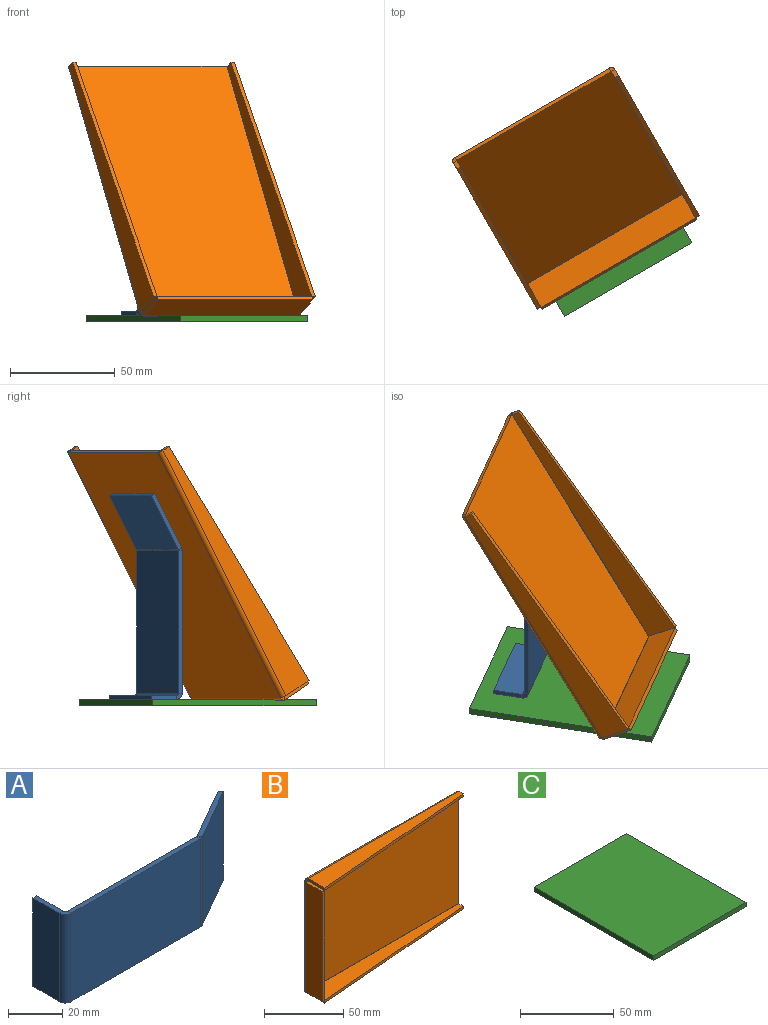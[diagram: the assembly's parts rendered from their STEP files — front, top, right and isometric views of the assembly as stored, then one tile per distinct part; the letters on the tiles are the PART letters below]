
ASSEMBLY  parts=3 mates=2
PART A: 22 faces, bbox 98x17x40 mm
  f0: plane 67.73x2mm, normal (0,0,1), area 135.5mm2, adj f2,f3,f10,f19
  f1: plane 67.73x2mm, normal (0,0,-1), area 135.5mm2, adj f2,f3,f9,f18
  f2: plane 67.73x40mm, normal (0,-1,0), area 2709.3mm2, adj f0,f1,f11,f20
  f3: plane 67.73x40mm, normal (0,1,0), area 2709.3mm2, adj f0,f1,f12,f21
  f4: plane 26.75x16.6mm, normal (0,0,1), area 59.5mm2, adj f6,f7,f8,f10
  f5: plane 26.75x16.6mm, normal (0,0,-1), area 59.5mm2, adj f6,f7,f8,f9
  f6: plane 40x1.73mm, normal (0.87,0.5,0), area 80mm2, adj f4,f5,f7,f8
  f7: plane 40x25.75mm, normal (0.5,-0.87,0), area 1189.3mm2, adj f4,f5,f6,f11
  f8: plane 40x25.75mm, normal (-0.5,0.87,0), area 1189.3mm2, adj f4,f5,f6,f12
  f9: plane 2.13x1.5mm, normal (0,0,-1), area 2.1mm2, adj f1,f5,f11,f12
  f10: plane 2.13x1.5mm, normal (0,0,1), area 2.1mm2, adj f0,f4,f11,f12
  f11: cylinder r=3mm len=40mm, axis (0,0,-1), area 62.8mm2, adj f2,f7,f9,f10
  f12: cylinder r=1mm len=40mm, axis (0,0,-1), area 20.9mm2, adj f3,f8,f9,f10
  f13: plane 14x2mm, normal (0,0,1), area 28mm2, adj f14,f16,f17,f19
  f14: plane 40x2mm, normal (0,1,0), area 80mm2, adj f13,f15,f16,f17
  f15: plane 14x2mm, normal (0,0,-1), area 28mm2, adj f14,f16,f17,f18
  f16: plane 40x14mm, normal (-1,0,0), area 560mm2, adj f13,f14,f15,f20
  f17: plane 40x14mm, normal (1,0,0), area 560mm2, adj f13,f14,f15,f21
  f18: plane 3x3mm, normal (0,0,-1), area 6.3mm2, adj f1,f15,f20,f21
  f19: plane 3x3mm, normal (0,0,1), area 6.3mm2, adj f0,f13,f20,f21
  f20: cylinder r=3mm len=40mm, axis (0,0,-1), area 188.5mm2, adj f2,f16,f18,f19
  f21: cylinder r=1mm len=40mm, axis (0,0,-1), area 62.8mm2, adj f3,f17,f18,f19
PART B: 34 faces, bbox 137x17x89 mm
  f0: plane 2x0.08mm, normal (0,1,0), area 0.2mm2, adj f1,f4,f5,f31
  f1: plane 14.9x2mm, normal (-1,0,0), area 29.8mm2, adj f0,f3,f4,f5
  f2: plane 3.9x2mm, normal (1,0,0), area 7.8mm2, adj f3,f4,f5,f30
  f3: plane 134.98x11mm, normal (0.08,-1,0), area 270.9mm2, adj f1,f2,f4,f5
  f4: plane 134.98x14.9mm, normal (0,0,-1), area 1268.8mm2, adj f0,f1,f2,f3,f32
  f5: plane 134.98x14.9mm, normal (0,0,1), area 1268.8mm2, adj f0,f1,f2,f3,f33
  f6: plane 3.9x2mm, normal (1,0,0), area 7.8mm2, adj f9,f10,f11,f26
  f7: plane 2x0.08mm, normal (0,1,0), area 0.2mm2, adj f8,f10,f11,f27
  f8: plane 14.9x2mm, normal (-1,0,0), area 29.8mm2, adj f7,f9,f10,f11
  f9: plane 134.98x11mm, normal (0.08,-1,0), area 270.9mm2, adj f6,f8,f10,f11
  f10: plane 134.98x14.9mm, normal (0,0,1), area 1268.8mm2, adj f6,f7,f8,f9,f28
  f11: plane 134.98x14.9mm, normal (0,0,-1), area 1268.8mm2, adj f6,f7,f8,f9,f29
  f12: plane 84.8x2mm, normal (1,0,0), area 169.6mm2, adj f13,f14,f26,f30
  f13: plane 134.9x84.8mm, normal (0,1,0), area 11439.5mm2, adj f12,f24,f28,f32
  f14: plane 134.9x84.8mm, normal (0,-1,0), area 11439.5mm2, adj f12,f25,f29,f33
  f15: plane 2x0.08mm, normal (0,1,0), area 0.2mm2, adj f16,f20,f21,f23
  f16: plane 14.9x2mm, normal (0,0,1), area 29.8mm2, adj f15,f19,f20,f21
  f17: plane 2x0.08mm, normal (0,1,0), area 0.2mm2, adj f18,f20,f21,f22
  f18: plane 14.9x2mm, normal (0,0,-1), area 29.8mm2, adj f17,f19,f20,f21
  f19: plane 84.96x2mm, normal (0,-1,0), area 169.9mm2, adj f16,f18,f20,f21
  f20: plane 84.96x14.9mm, normal (-1,0,0), area 1265.9mm2, adj f15,f16,f17,f18,f19,f24
  f21: plane 84.96x14.9mm, normal (1,0,0), area 1265.9mm2, adj f15,f16,f17,f18,f19,f25
  f22: plane 2.1x2.1mm, normal (0,0,-1), area 3.5mm2, adj f17,f24,f25,f31
  f23: plane 2.1x2.1mm, normal (0,0,1), area 3.5mm2, adj f15,f24,f25,f27
  f24: cylinder r=2.1mm len=84.8mm, axis (0,0,-1), area 279.7mm2, adj f13,f20,f22,f23
  f25: cylinder r=0.1mm len=84.8mm, axis (0,0,-1), area 13.3mm2, adj f14,f21,f22,f23
  f26: plane 2.1x2.1mm, normal (1,0,0), area 3.5mm2, adj f6,f12,f28,f29
  f27: plane 2.1x2.1mm, normal (-1,0,0), area 3.5mm2, adj f7,f23,f28,f29
  f28: cylinder r=2.1mm len=134.9mm, axis (1,0,0), area 445mm2, adj f10,f13,f26,f27
  f29: cylinder r=0.1mm len=134.9mm, axis (1,0,0), area 21.2mm2, adj f11,f14,f26,f27
  f30: plane 2.1x2.1mm, normal (1,0,0), area 3.5mm2, adj f2,f12,f32,f33
  f31: plane 2.1x2.1mm, normal (-1,0,0), area 3.5mm2, adj f0,f22,f32,f33
  f32: cylinder r=2.1mm len=134.9mm, axis (1,0,0), area 445mm2, adj f4,f13,f30,f31
  f33: cylinder r=0.1mm len=134.9mm, axis (1,0,0), area 21.2mm2, adj f5,f14,f30,f31
PART C: 6 faces, bbox 70x90x3 mm
  f0: plane 70x3mm, normal (0,1,0), area 210mm2, adj f1,f3,f4,f5
  f1: plane 90x3mm, normal (-1,0,0), area 270mm2, adj f0,f2,f4,f5
  f2: plane 70x3mm, normal (0,-1,0), area 210mm2, adj f1,f3,f4,f5
  f3: plane 90x3mm, normal (1,0,0), area 270mm2, adj f0,f2,f4,f5
  f4: plane 90x70mm, normal (0,0,1), area 6300mm2, adj f0,f1,f2,f3
  f5: plane 90x70mm, normal (0,0,-1), area 6300mm2, adj f0,f1,f2,f3
PLACE A rot(axis=(0.25,-0.94,0.25),93.8deg) t=(-33.36,9.79,33.35)mm
PLACE B rot(axis=(0,-0.89,0.45),104.5deg) t=(14.95,-28.9,11.08)mm
PLACE C rot(axis=(0,0,-1),150deg) t=(-66.05,-17.07,-1.04)mm
MATE fastened A.f7 <-> B.f13  axis (0.43,-0.75,0.5) through (-53.6,4.84,87.06)mm
MATE fastened C.f4 <-> A.f16  axis (0,0,1) through (-39.68,-19.26,1.96)mm
